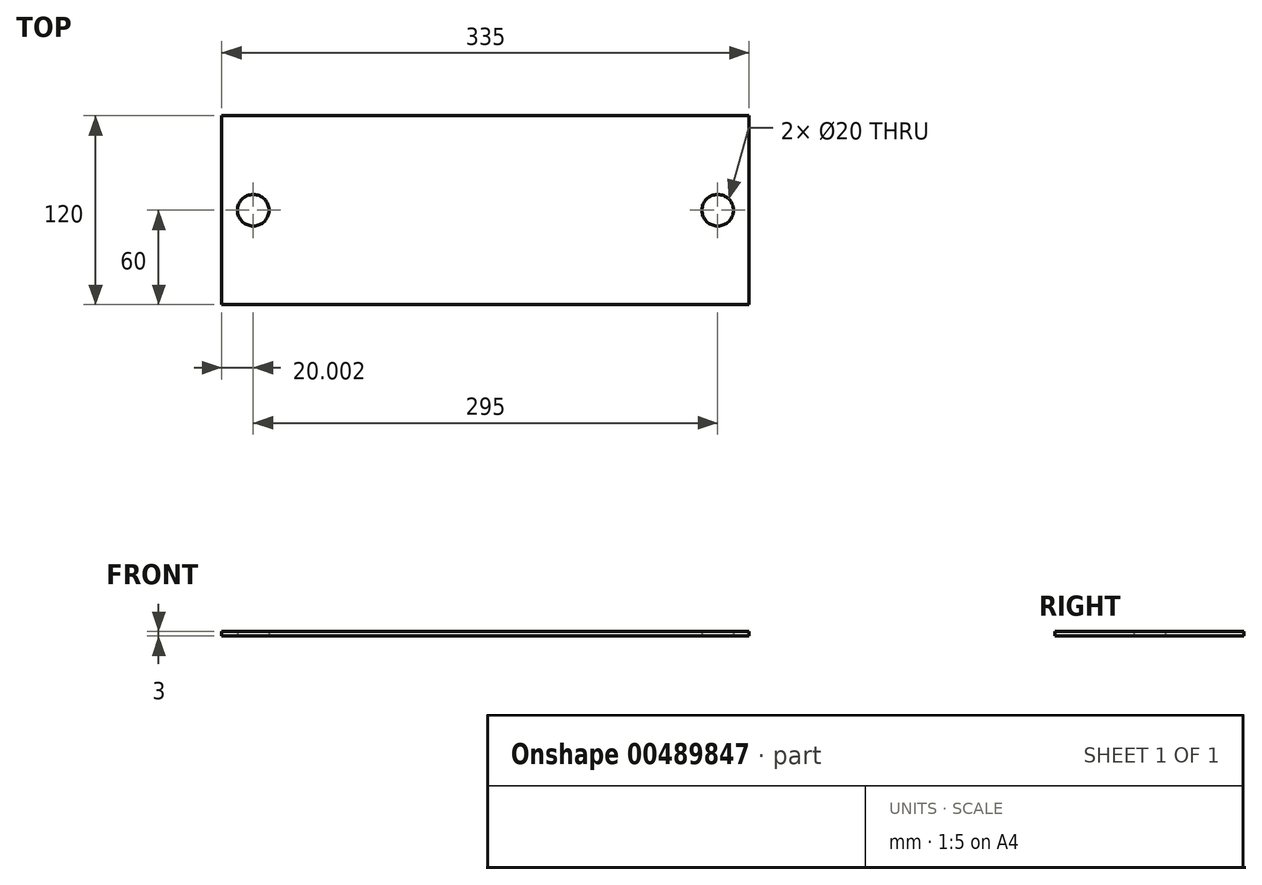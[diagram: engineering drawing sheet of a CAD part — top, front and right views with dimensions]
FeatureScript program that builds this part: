
annotation { "Feature Type Name" : "Feature", "Feature Type Description" : "" }
export const myFeature = defineFeature(function(context is Context, id is Id, definition is map)
    precondition{}
    {
        {
            var Q0;
            Q0=qCreatedBy(makeId("Top.planeOp"),FACE);
            var sketch = newSketch(context, id + "F0", { "sketchPlane" : qUnion([Q0])});
            skLineSegment(sketch, "E0.bottom", {"start": v(-175.32, 60) * mm, "end": v(159.68, 60) * mm});
            skLineSegment(sketch, "E0.top", {"start": v(-175.32, -60) * mm, "end": v(159.68, -60) * mm});
            skLineSegment(sketch, "E0.left", {"start": v(-175.32, 60) * mm, "end": v(-175.32, -60) * mm});
            skLineSegment(sketch, "E0.right", {"start": v(159.68, 60) * mm, "end": v(159.68, -60) * mm});
            skCircle(sketch, "E1", {"center": v(-155.32, 0) * mm, "radius": 10 * mm});
            skCircle(sketch, "E2", {"center": v(139.68, 0) * mm, "radius": 10 * mm});
            skSolve(sketch);
        }
        {
            var Q0;
            Q0=makeQuery(id+"F0.imprint","IMPRINT",FACE,{"disambiguationData":[TD([[makeQuery(id+"F0.imprint","IMPRINT",EDGE,{"derivedFrom":sQuery(id+"F0.wireOp",EDGE,"E0.bottom")}),-1.0]])]});
            extrude(context, id + "F1", {"entities" : qUnion([Q0]), "depth" : 3 * mm});
        }
    });
